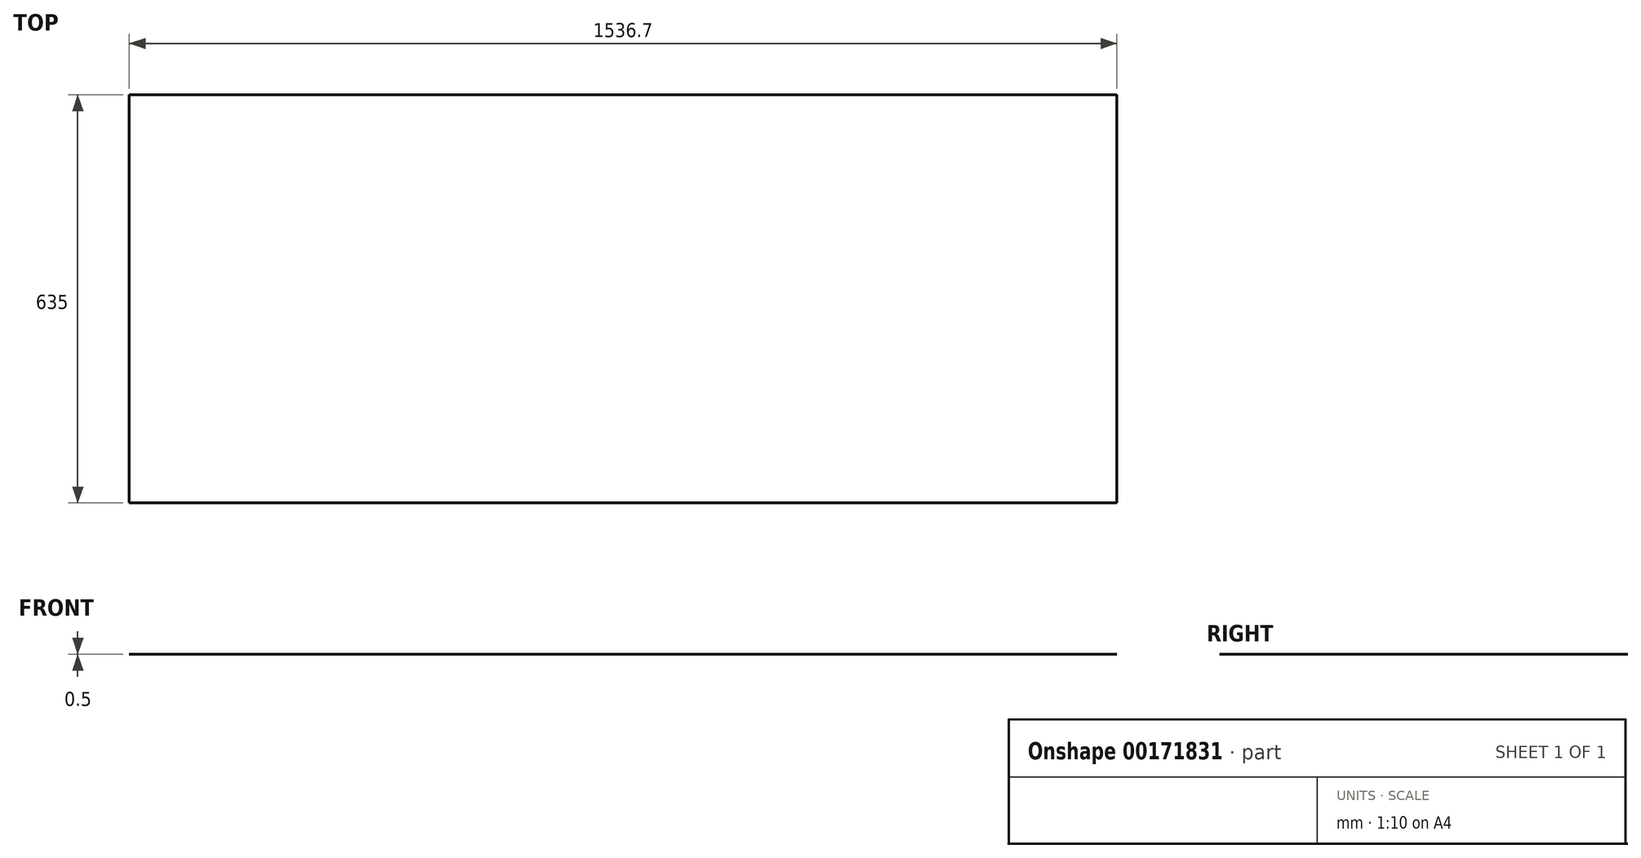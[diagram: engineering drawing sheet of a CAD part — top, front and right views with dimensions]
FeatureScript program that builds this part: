
annotation { "Feature Type Name" : "Feature", "Feature Type Description" : "" }
export const myFeature = defineFeature(function(context is Context, id is Id, definition is map)
    precondition{}
    {
        {
            var Q0;
            Q0=qCreatedBy(makeId("Top.planeOp"),FACE);
            var sketch = newSketch(context, id + "F0", { "sketchPlane" : qUnion([Q0])});
            skLineSegment(sketch, "E0.bottom", {"start": v(768.35, 317.5) * mm, "end": v(-768.35, 317.5) * mm});
            skLineSegment(sketch, "E0.top", {"start": v(768.35, -317.5) * mm, "end": v(-768.35, -317.5) * mm});
            skLineSegment(sketch, "E0.left", {"start": v(768.35, 317.5) * mm, "end": v(768.35, -317.5) * mm});
            skLineSegment(sketch, "E0.right", {"start": v(-768.35, 317.5) * mm, "end": v(-768.35, -317.5) * mm});
            skPoint(sketch, "E0.middle", {"position": v(0, 0) * mm});
            skSolve(sketch);
        }
        {
            assignVariable(context, id + "F1", {"name" : "board_thickness", "anyValue" : .5});
        }
        {
            var Q0;
            Q0=makeQuery(id+"F0.imprint","IMPRINT",FACE,{"disambiguationData":[TD([[makeQuery(id+"F0.imprint","IMPRINT",EDGE,{"derivedFrom":sQuery(id+"F0.wireOp",EDGE,"E0.bottom")}),1.0]])]});
            extrude(context, id + "F2", {"entities" : qUnion([Q0]), "depth" : (getVariable(context, 'board_thickness')) * mm});
        }
    });
